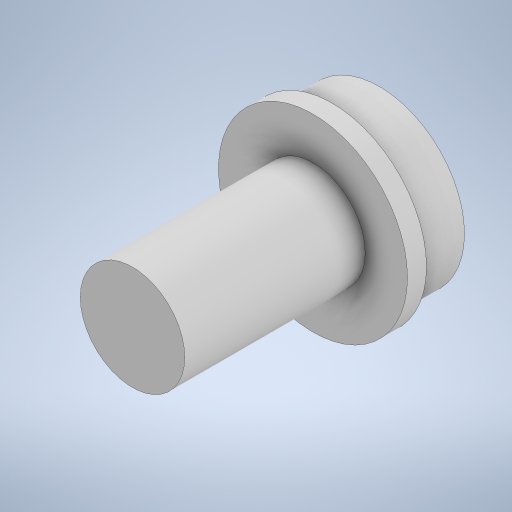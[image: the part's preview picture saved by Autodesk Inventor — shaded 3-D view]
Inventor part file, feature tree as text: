
AUTODESK INVENTOR PART (.ipt)
format: ipt  version: 2024.2 (Build 282272000, 272)  size: 232,448 bytes
history: native  units: mm
features: extrude x3, other x1, sketch x1
ambient origin geometry x8: Origin, YZ Plane, XZ Plane, XY Plane, X Axis, Y Axis, Z Axis, Center Point
bodies: Body1 (feature_tree)
feature tree (5):
  other  "Твердое тело1"
  sketch  "Эскиз1"
  extrude  "Выдавливание1"  Depth=17.9mm
  extrude  "Выдавливание2"  Depth=19.9mm
  extrude  "Выдавливание3"  Depth=11.0mm
